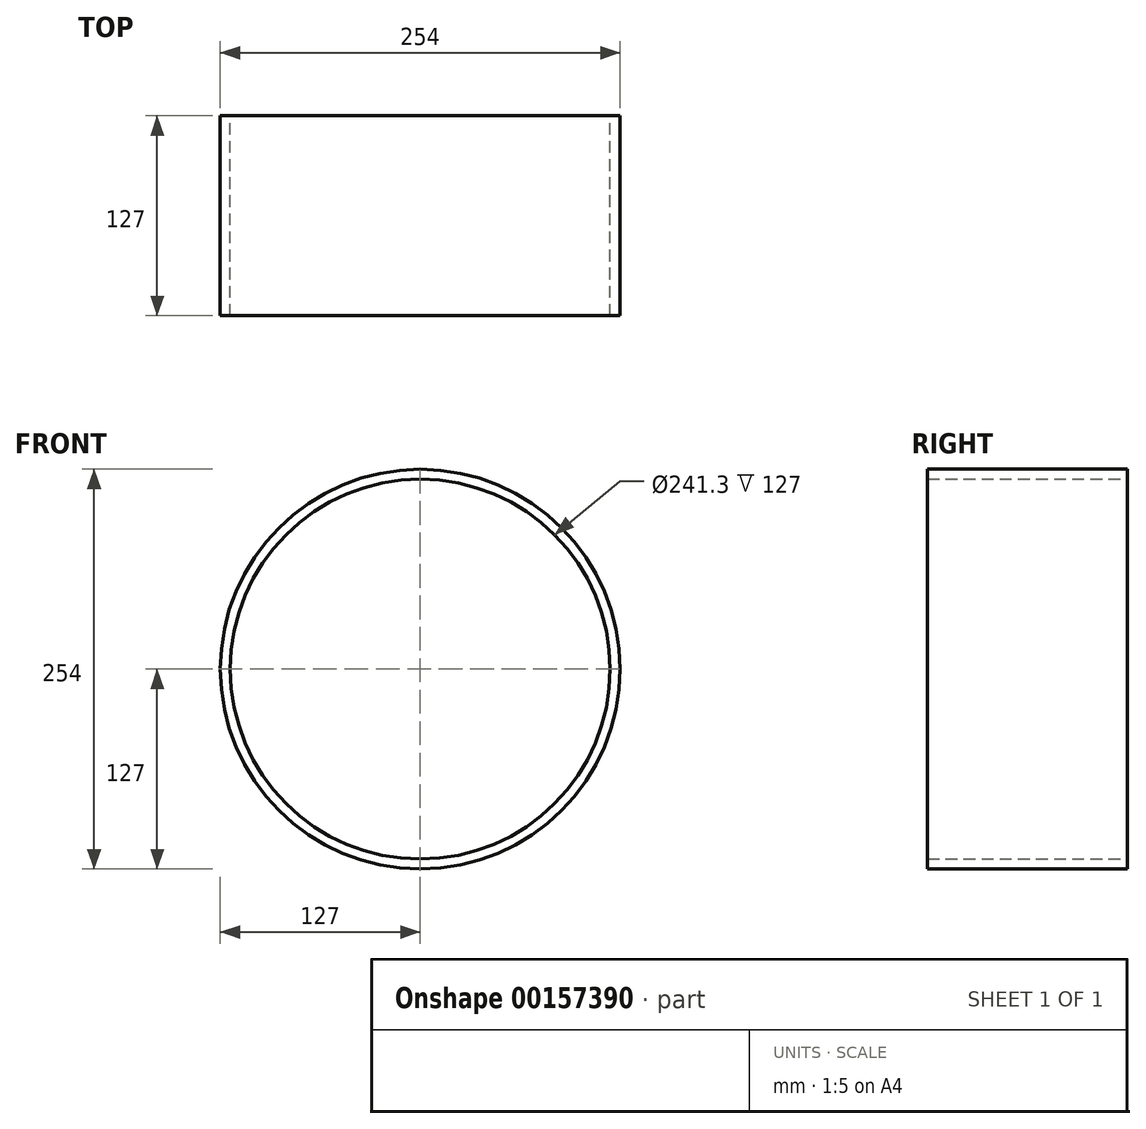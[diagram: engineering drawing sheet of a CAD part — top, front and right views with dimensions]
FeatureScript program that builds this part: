
annotation { "Feature Type Name" : "Feature", "Feature Type Description" : "" }
export const myFeature = defineFeature(function(context is Context, id is Id, definition is map)
    precondition{}
    {
        {
            var Q0;
            Q0=qCreatedBy(makeId("Front.planeOp"),FACE);
            var sketch = newSketch(context, id + "F0", { "sketchPlane" : qUnion([Q0])});
            skCircle(sketch, "E0", {"center": v(0, 0) * mm, "radius": 127 * mm});
            skCircle(sketch, "E1", {"center": v(0, 0) * mm, "radius": 120.65 * mm});
            skSolve(sketch);
        }
        {
            var Q0;
            Q0 = qSketchRegion(id + "F0", true);
            extrude(context, id + "F1", {"entities" : qUnion([Q0]), "depth" : 127 * mm});
        }
    });
